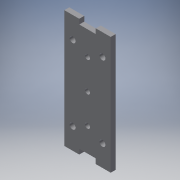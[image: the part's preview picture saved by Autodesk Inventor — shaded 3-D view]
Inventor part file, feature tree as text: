
AUTODESK INVENTOR PART (.ipt)
format: ipt  version: 2018 (Build 220112000, 112)  size: 134,144 bytes
history: native  units: in
note: dims shown in document units (in); Inventor stores cm internally (conversion verified against a paired STEP export)
features: reference x10, other x7, extrude x3, sketch x3, projected_geometry x1
ambient origin geometry x8: Origin, YZ Plane, XZ Plane, XY Plane, X Axis, Y Axis, Z Axis, Center Point
bodies: Solid1 (feature_tree)
feature tree (24):
  extrude  "Extrusion1"  Depth=0.1181in
  extrude  "Extrusion2"  Depth=0.1181in
  extrude  "Extrusion3"  Depth=0.1181in
  sketch  "Sketch1"  dims[d0=0.1181in d1=0.0in d2=0.1181in]
  reference  "Reference1"
  reference  "Reference2"
  reference  "Reference3"
  reference  "Reference4"
  reference  "Reference5"
  reference  "Reference6"
  sketch  "Sketch2"  dims[d3=0.1181in d4=0.1181in]
  projected_geometry  "Projected Loop1"
  sketch  "Sketch3"  dims[d5=0.7087in d6=0.7087in d7=0.1181in d8=0.0in d9=0.1181in d10=0.0in]
  reference  "Reference7"
  reference  "Reference8"
  reference  "Reference9"
  reference  "Reference10"
  other  "Camera pan and tilt assembly.iam"
  other  "Camera mount side bars:1"
  other  "Camera mount side bars:2"
  other  "Angle bracket short:11"
  other  "Angle bracket short:9"
  other  "Angle bracket short:10"
  other  "Angle bracket short:12"
